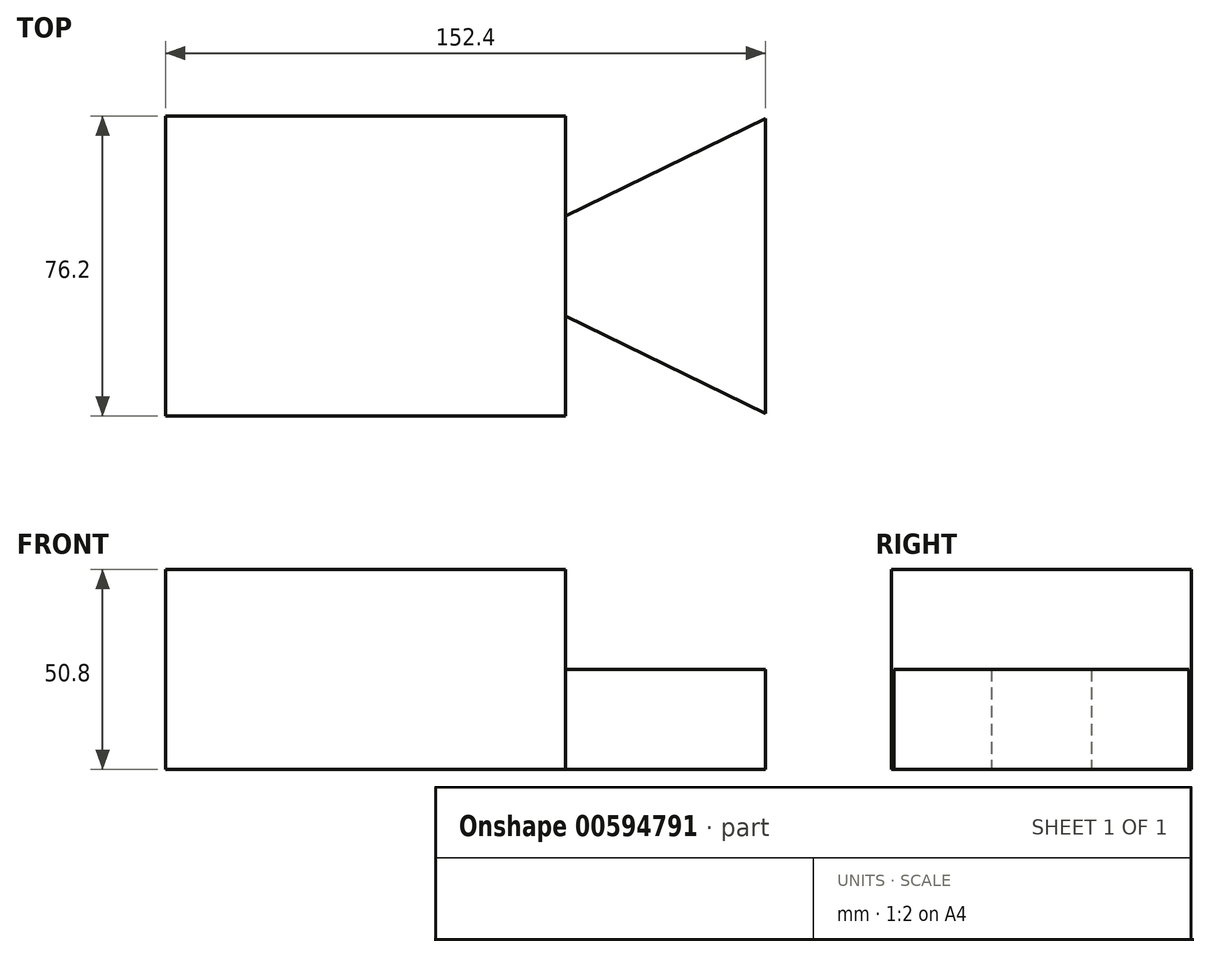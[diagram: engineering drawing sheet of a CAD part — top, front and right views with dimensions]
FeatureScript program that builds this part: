
annotation { "Feature Type Name" : "Feature", "Feature Type Description" : "" }
export const myFeature = defineFeature(function(context is Context, id is Id, definition is map)
    precondition{}
    {
        {
            var Q0;
            Q0=qCreatedBy(makeId("Top.planeOp"),FACE);
            var sketch = newSketch(context, id + "F0", { "sketchPlane" : qUnion([Q0])});
            skLineSegment(sketch, "E0", {"start": v(-63.56, 51.75) * mm, "end": v(-63.56, -24.45) * mm});
            skLineSegment(sketch, "E1", {"start": v(-63.56, 51.75) * mm, "end": v(38.04, 51.75) * mm});
            skLineSegment(sketch, "E2", {"start": v(38.04, 51.75) * mm, "end": v(38.04, -24.45) * mm});
            skLineSegment(sketch, "E3", {"start": v(-63.56, -24.45) * mm, "end": v(38.04, -24.45) * mm});
            skLineSegment(sketch, "E4", {"start": v(88.84, 51.12) * mm, "end": v(38.04, 26.35) * mm});
            skLineSegment(sketch, "E5", {"start": v(38.04, 0.95) * mm, "end": v(88.84, -23.81) * mm});
            skLineSegment(sketch, "E6", {"start": v(88.84, 51.12) * mm, "end": v(88.84, -23.81) * mm});
            skSolve(sketch);
        }
        {
            var Q0;
            {var subQ0=sQuery(id+"F0.wireOp",EDGE,"E4");Q0=makeQuery(id+"F0.imprint","IMPRINT",FACE,{"disambiguationData":[TD([[makeQuery(id+"F0.imprint","IMPRINT",EDGE,{"derivedFrom":subQ0}),1.0]])]});}
            extrude(context, id + "F1", {"entities" : qUnion([Q0]), "depth" : 25.4 * mm, "offsetDistance" : 25.4 * mm});
        }
        {
            var Q0;
            Q0=makeQuery(id+"F0.imprint","IMPRINT",FACE,{"disambiguationData":[TD([[makeQuery(id+"F0.imprint","IMPRINT",EDGE,{"derivedFrom":sQuery(id+"F0.wireOp",EDGE,"E0")}),1.0]])]});
            extrude(context, id + "F2", {"entities" : qUnion([Q0]), "operationType" : NewBodyOperationType.ADD, "depth" : 50.8 * mm, "offsetDistance" : 25.4 * mm});
        }
    });
